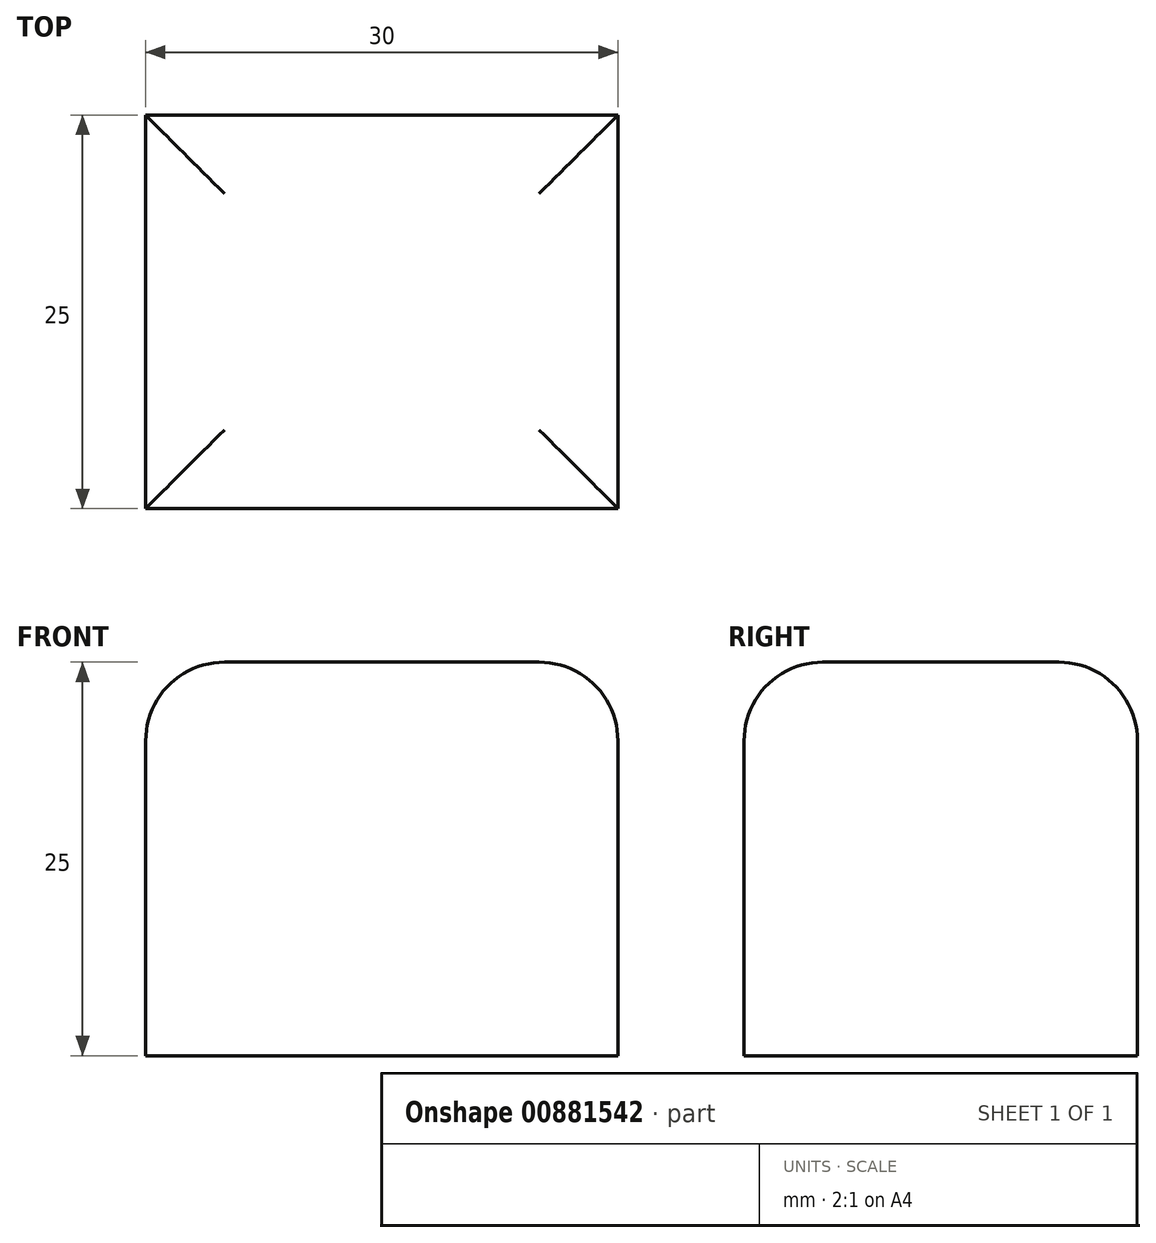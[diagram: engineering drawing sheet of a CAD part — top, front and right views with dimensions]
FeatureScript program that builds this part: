
annotation { "Feature Type Name" : "Feature", "Feature Type Description" : "" }
export const myFeature = defineFeature(function(context is Context, id is Id, definition is map)
    precondition{}
    {
        {
            var Q0;
            Q0=qCreatedBy(makeId("Top.planeOp"),FACE);
            var sketch = newSketch(context, id + "F0", { "sketchPlane" : qUnion([Q0])});
            skLineSegment(sketch, "E0.bottom", {"start": v(-10, 12) * mm, "end": v(20, 12) * mm});
            skLineSegment(sketch, "E0.top", {"start": v(-10, -13) * mm, "end": v(20, -13) * mm});
            skLineSegment(sketch, "E0.left", {"start": v(-10, 12) * mm, "end": v(-10, -13) * mm});
            skLineSegment(sketch, "E0.right", {"start": v(20, 12) * mm, "end": v(20, -13) * mm});
            skSolve(sketch);
        }
        {
            var Q0;
            Q0 = qSketchRegion(id + "F0", true);
            extrude(context, id + "F1", {"entities" : qUnion([Q0]), "depth" : 25 * mm, "offsetDistance" : 25 * mm});
        }
        {
            var Q0;
            Q0=makeQuery(id+"F1.opExtrude","CAP_EDGE",EDGE,{"disambiguationData":[OSD([sQuery(id+"F0.wireOp",EDGE,"E0.left")])],"isStart":false});
            var Q1;
            Q1=makeQuery(id+"F1.opExtrude","CAP_EDGE",EDGE,{"disambiguationData":[OSD([sQuery(id+"F0.wireOp",EDGE,"E0.right")])],"isStart":false});
            var Q2;
            Q2=makeQuery(id+"F1.opExtrude","CAP_EDGE",EDGE,{"disambiguationData":[OSD([sQuery(id+"F0.wireOp",EDGE,"E0.bottom")])],"isStart":false});
            var Q3;
            Q3=makeQuery(id+"F1.opExtrude","CAP_EDGE",EDGE,{"disambiguationData":[OSD([sQuery(id+"F0.wireOp",EDGE,"E0.top")])],"isStart":false});
            fillet(context, id + "F2", {"entities" : qUnion([Q0, Q1, Q2, Q3]), "radius" : 5 * mm, "tangentPropagation" : true, "allowEdgeOverflow" : false});
        }
    });
